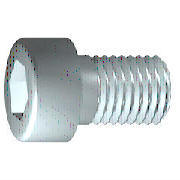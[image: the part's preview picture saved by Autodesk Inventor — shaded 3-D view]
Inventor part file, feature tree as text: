
AUTODESK INVENTOR PART (.ipt)
format: ipt  version: 2020 (Build 240168000, 168)  size: 193,536 bytes
history: native  units: mm (DEFAULTED — no unit token found)
features: sketch x2, other x1, extrude x1, plane x1, fillet x1
ambient origin geometry x7: Origin, YZ Plane, XY Plane, X Axis, Y Axis, Z Axis, Center Point
bodies: Solid1 (feature_tree)
feature tree (6):
  other  "Bryła"
  extrude  "Szczelina"  Depth=27.0mm
  plane  "Work Plane1"
  fillet  "Fillet2"  Radius=0.61355mm
  sketch  "Szkic1"
  sketch  "Szkic2"
